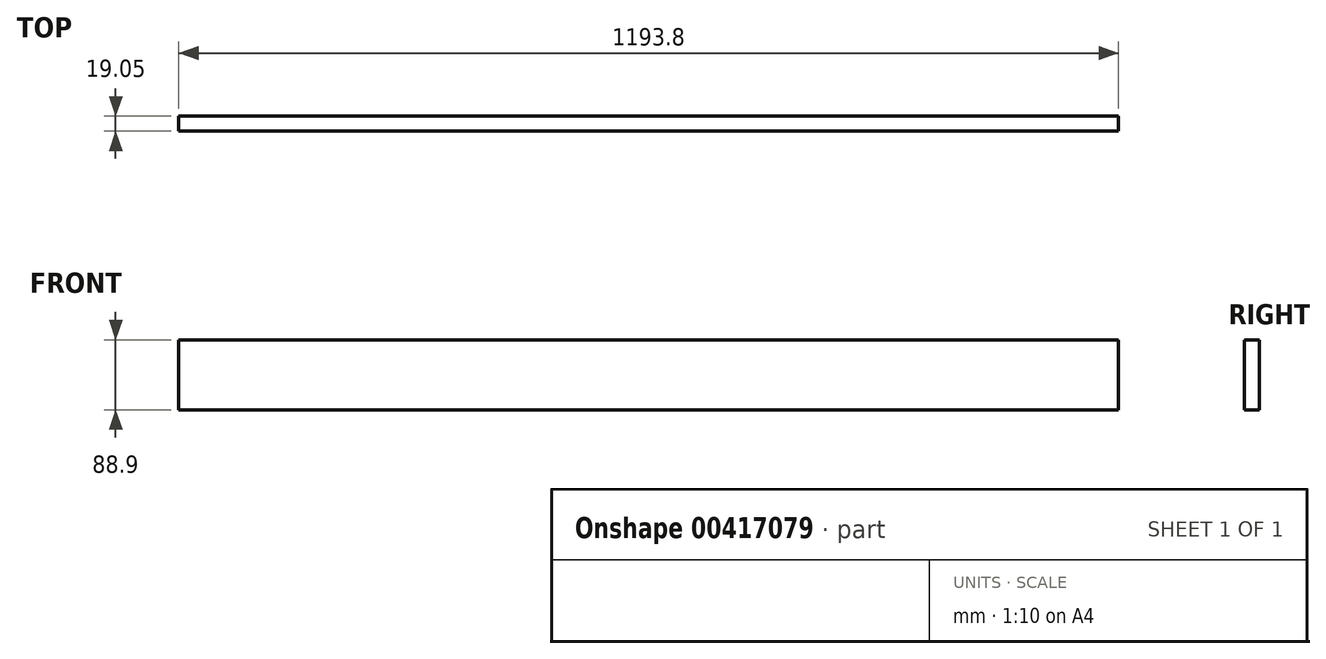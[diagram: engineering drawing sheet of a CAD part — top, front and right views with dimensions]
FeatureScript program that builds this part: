
annotation { "Feature Type Name" : "Feature", "Feature Type Description" : "" }
export const myFeature = defineFeature(function(context is Context, id is Id, definition is map)
    precondition{}
    {
        {
            var Q0;
            Q0=qCreatedBy(makeId("Front.planeOp"),FACE);
            var sketch = newSketch(context, id + "F0", { "sketchPlane" : qUnion([Q0])});
            skLineSegment(sketch, "E0.bottom", {"start": v(0, 0) * mm, "end": v(1193.8, 0) * mm});
            skLineSegment(sketch, "E0.top", {"start": v(0, -88.9) * mm, "end": v(1193.8, -88.9) * mm});
            skLineSegment(sketch, "E0.left", {"start": v(0, 0) * mm, "end": v(0, -88.9) * mm});
            skLineSegment(sketch, "E0.right", {"start": v(1193.8, 0) * mm, "end": v(1193.8, -88.9) * mm});
            skSolve(sketch);
        }
        {
            var Q0;
            Q0 = qSketchRegion(id + "F0", true);
            extrude(context, id + "F1", {"entities" : qUnion([Q0]), "depth" : 19.05 * mm});
        }
    });
